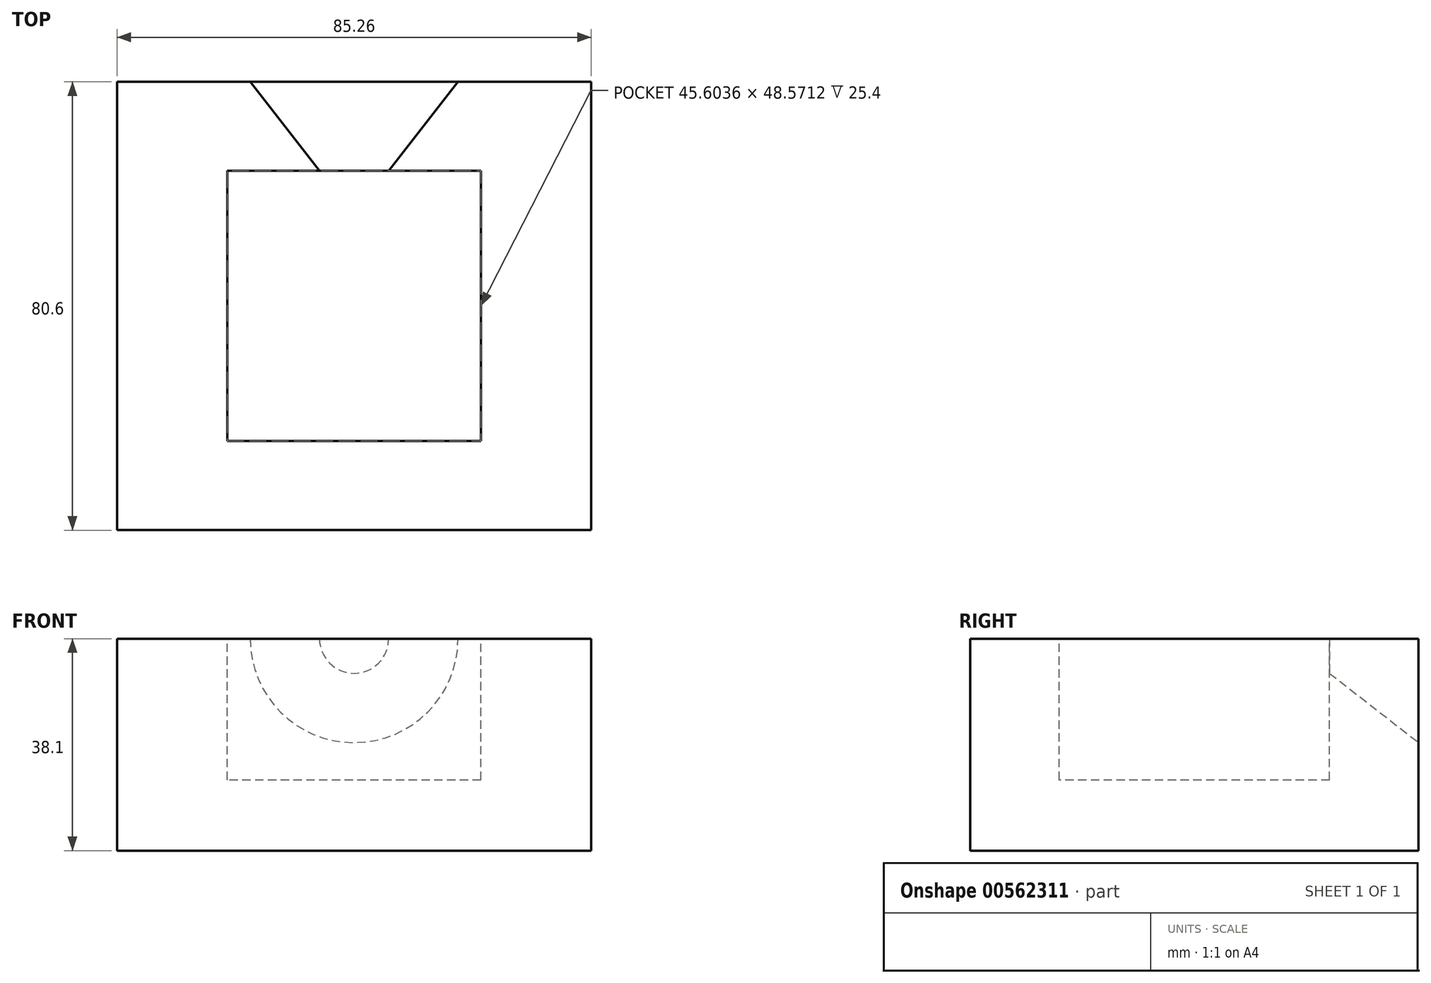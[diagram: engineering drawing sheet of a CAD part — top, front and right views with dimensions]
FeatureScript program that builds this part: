
annotation { "Feature Type Name" : "Feature", "Feature Type Description" : "" }
export const myFeature = defineFeature(function(context is Context, id is Id, definition is map)
    precondition{}
    {
        {
            var Q0;
            Q0=qCreatedBy(makeId("Top.planeOp"),FACE);
            var sketch = newSketch(context, id + "F0", { "sketchPlane" : qUnion([Q0])});
            skLineSegment(sketch, "E0.bottom", {"start": v(42.63, 40.3) * mm, "end": v(-42.63, 40.3) * mm});
            skLineSegment(sketch, "E0.top", {"start": v(42.63, -40.3) * mm, "end": v(-42.63, -40.3) * mm});
            skLineSegment(sketch, "E0.left", {"start": v(42.63, 40.3) * mm, "end": v(42.63, -40.3) * mm});
            skLineSegment(sketch, "E0.right", {"start": v(-42.63, 40.3) * mm, "end": v(-42.63, -40.3) * mm});
            skPoint(sketch, "E0.middle", {"position": v(0, 0) * mm});
            skSolve(sketch);
        }
        {
            var Q0;
            Q0=makeQuery(id+"F0.imprint","IMPRINT",FACE,{"disambiguationData":[TD([[makeQuery(id+"F0.imprint","IMPRINT",EDGE,{"derivedFrom":sQuery(id+"F0.wireOp",EDGE,"E0.bottom")}),1.0]])]});
            extrude(context, id + "F1", {"entities" : qUnion([Q0]), "depth" : 38.1 * mm, "offsetDistance" : 25.4 * mm});
        }
        {
            var Q0;
            Q0=makeQuery(id+"F1.opExtrude","CAP_FACE",FACE,{"disambiguationData":[OSD([sQuery(id+"F0.wireOp",EDGE,"E0.bottom"),sQuery(id+"F0.wireOp",EDGE,"E0.top"),sQuery(id+"F0.wireOp",EDGE,"E0.left"),sQuery(id+"F0.wireOp",EDGE,"E0.right")])],"isStart":false});
            var sketch = newSketch(context, id + "F2", { "sketchPlane" : qUnion([Q0])});
            skLineSegment(sketch, "E1.bottom", {"start": v(22.8, 24.29) * mm, "end": v(-22.8, 24.29) * mm});
            skLineSegment(sketch, "E1.top", {"start": v(22.8, -24.29) * mm, "end": v(-22.8, -24.29) * mm});
            skLineSegment(sketch, "E1.left", {"start": v(22.8, 24.29) * mm, "end": v(22.8, -24.29) * mm});
            skLineSegment(sketch, "E1.right", {"start": v(-22.8, 24.29) * mm, "end": v(-22.8, -24.29) * mm});
            skPoint(sketch, "E1.middle", {"position": v(0, 0) * mm});
            skSolve(sketch);
        }
        {
            var Q0;
            Q0=makeQuery(id+"F2.imprint","IMPRINT",FACE,{"disambiguationData":[TD([[makeQuery(id+"F2.imprint","IMPRINT",EDGE,{"derivedFrom":sQuery(id+"F2.wireOp",EDGE,"E1.bottom")}),1.0]])]});
            extrude(context, id + "F3", {"entities" : qUnion([Q0]), "operationType" : NewBodyOperationType.REMOVE, "oppositeDirection" : true, "depth" : 25.4 * mm, "offsetDistance" : 25.4 * mm});
        }
        {
            var Q0;
            Q0=makeQuery(id+"F1.opExtrude","SWEPT_FACE",FACE,{"disambiguationData":[OSD([sQuery(id+"F0.wireOp",EDGE,"E0.bottom")])]});
            var sketch = newSketch(context, id + "F4", { "sketchPlane" : qUnion([Q0])});
            skArc(sketch, "E2", {"start": v(-18.68, 38.1) * mm, "mid": v(0, 19.42) * mm, "end": v(18.68, 38.1) * mm});
            skLineSegment(sketch, "E3", {"start": v(18.68, 38.1) * mm, "end": v(-18.68, 38.1) * mm});
            skSolve(sketch);
        }
        {
            var Q0;
            Q0=makeQuery(id+"F3.boolean.opBoolean","COPY",FACE,{"derivedFrom":makeQuery(id+"F3.opExtrude","SWEPT_FACE",FACE,{"disambiguationData":[OSD([sQuery(id+"F2.wireOp",EDGE,"E1.bottom")])]})});
            var sketch = newSketch(context, id + "F5", { "sketchPlane" : qUnion([Q0])});
            skArc(sketch, "E4", {"start": v(-6.22, 38.1) * mm, "mid": v(0, 31.88) * mm, "end": v(6.22, 38.1) * mm});
            skLineSegment(sketch, "E5", {"start": v(-6.22, 38.1) * mm, "end": v(6.22, 38.1) * mm});
            skSolve(sketch);
        }
        {
            var Q1;
            {var subQ0=sQuery(id+"F4.wireOp",EDGE,"E2");var subQ1=makeQuery(id+"F1.opExtrude","CAP_EDGE",EDGE,{"disambiguationData":[OSD([sQuery(id+"F0.wireOp",EDGE,"E0.bottom")])],"isStart":false});var subQ2=makeQuery(id+"F4.imprint","INTERSECT",VERTEX,{"disambiguationData":[OD(0.0)],"derivedFrom":[subQ1,subQ0]});Q1=makeQuery(id+"F4.imprint","IMPRINT",FACE,{"disambiguationData":[TD([[makeQuery(id+"F4.imprint","IMPRINT",EDGE,{"disambiguationData":[TD([[subQ2,1.0]])],"derivedFrom":subQ0}),1.0]])]});}
            var Q2;
            {var subQ0=sQuery(id+"F5.wireOp",EDGE,"E4");var subQ1=makeQuery(id+"F3.boolean.opBoolean","COPY",EDGE,{"derivedFrom":makeQuery(id+"F3.opExtrude","CAP_EDGE",EDGE,{"disambiguationData":[OSD([sQuery(id+"F2.wireOp",EDGE,"E1.bottom")])],"isStart":true})});var subQ2=makeQuery(id+"F5.imprint","INTERSECT",VERTEX,{"disambiguationData":[OD(0.0)],"derivedFrom":[subQ1,subQ0]});Q2=makeQuery(id+"F5.imprint","IMPRINT",FACE,{"disambiguationData":[TD([[makeQuery(id+"F5.imprint","IMPRINT",EDGE,{"disambiguationData":[TD([[subQ2,-1.0]])],"derivedFrom":subQ0}),1.0]])]});}
            var Q3;
            Q3 = qConstructionFilter(qBodyType(qCreatedBy(id + "F7" ,EDGE), BodyType.WIRE), ConstructionObject.NO);
            loft(context, id + "F6", {"operationType" : NewBodyOperationType.REMOVE, "addGuides" : true, "sheetProfilesArray" : [{ "sheetProfileEntities" : qUnion([Q1]) }, { "sheetProfileEntities" : qUnion([Q2]) }], "guidesArray" : [{ "guideEntities" : qUnion([Q3]), "guideDerivativeType" : LoftGuideDerivativeType.DEFAULT, "guideDerivativeMagnitude" : 1 }]});
        }
    });
